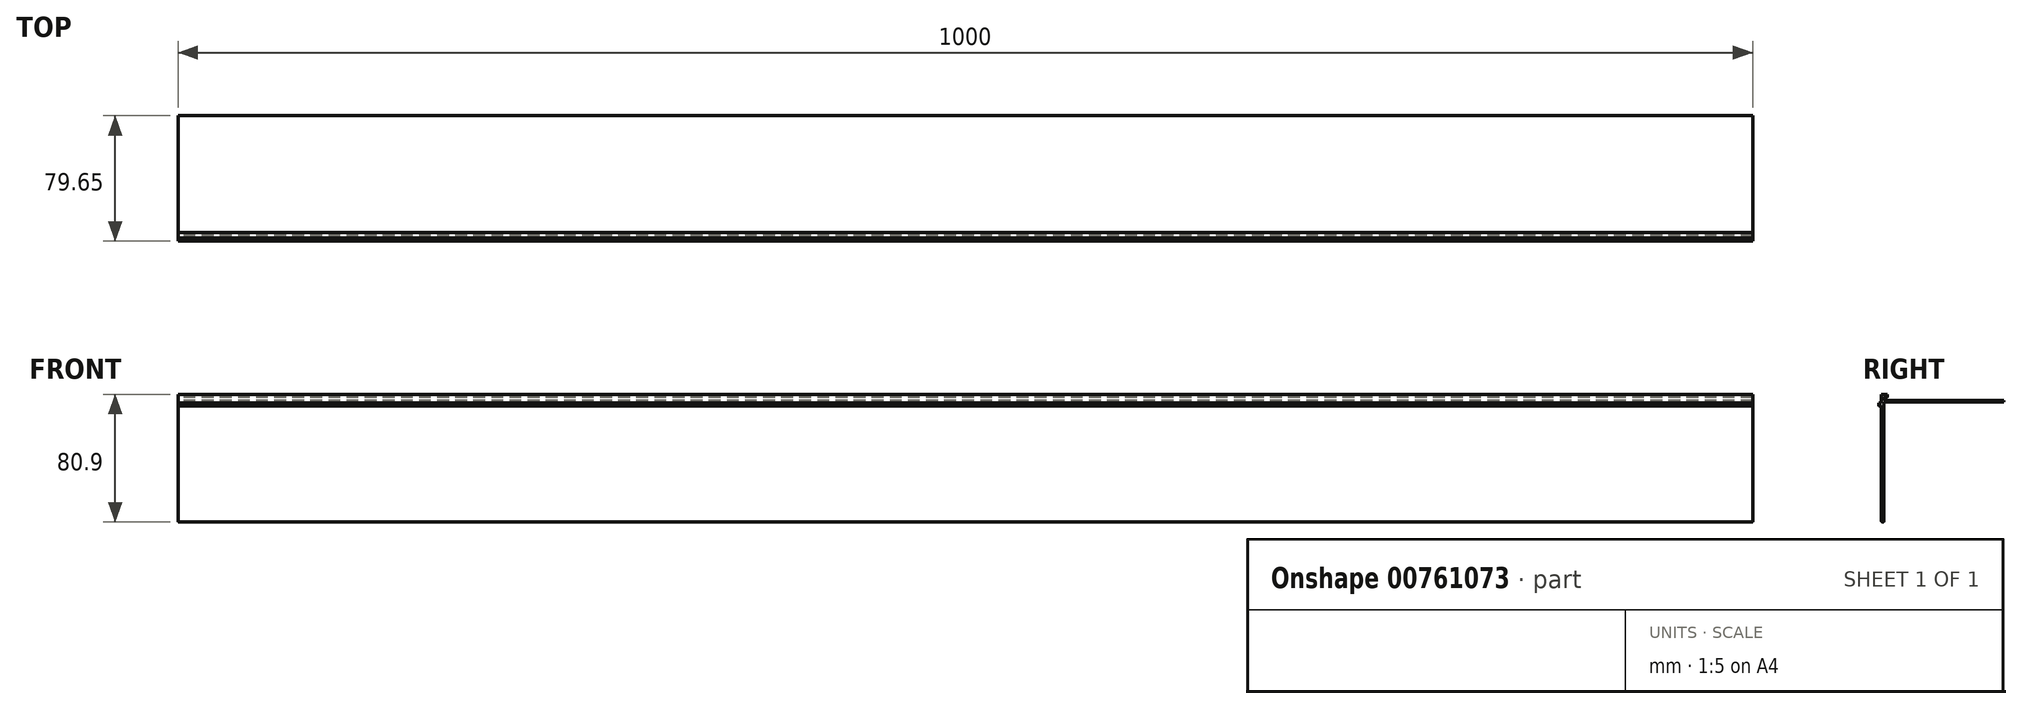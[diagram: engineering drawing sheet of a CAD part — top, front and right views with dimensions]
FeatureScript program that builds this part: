
annotation { "Feature Type Name" : "Feature", "Feature Type Description" : "" }
export const myFeature = defineFeature(function(context is Context, id is Id, definition is map)
    precondition{}
    {
        {
            var Q0;
            Q0=qCreatedBy(makeId("Right.planeOp"),FACE);
            var sketch = newSketch(context, id + "F0", { "sketchPlane" : qUnion([Q0])});
            skLineSegment(sketch, "E0", {"start": v(0, 0.5) * mm, "end": v(0, 73.95) * mm});
            skLineSegment(sketch, "E1", {"start": v(0, 80.9) * mm, "end": v(3.6, 80.9) * mm});
            skLineSegment(sketch, "E2", {"start": v(3.6, 80.9) * mm, "end": v(3.6, 79.3) * mm});
            skPoint(sketch, "E3.endSnap0", {"position": v(-2.18, 15.6) * mm});
            skLineSegment(sketch, "E4", {"start": v(1.6, 79.3) * mm, "end": v(1.6, 77.2) * mm});
            skLineSegment(sketch, "E5", {"start": v(1.6, 77.2) * mm, "end": v(77.8, 77.2) * mm});
            skLineSegment(sketch, "E6", {"start": v(77.8, 77.2) * mm, "end": v(77.8, 76.2) * mm});
            skLineSegment(sketch, "E7", {"start": v(77.8, 76.2) * mm, "end": v(1.6, 76.2) * mm});
            skLineSegment(sketch, "E8", {"start": v(1.6, 76.2) * mm, "end": v(1.6, 0.5) * mm});
            skLineSegment(sketch, "E9", {"start": v(1.1, 0) * mm, "end": v(0.5, 0) * mm});
            skPoint(sketch, "E10.visualSharp", {"position": v(1.6, 0) * mm});
            skArc(sketch, "E10.filletArc", {"start": v(1.1, 0) * mm, "mid": v(1.45, 0.15) * mm, "end": v(1.6, 0.5) * mm});
            skPoint(sketch, "E11.visualSharp", {"position": v(0, 0) * mm});
            skArc(sketch, "E11.filletArc", {"start": v(0, 0.5) * mm, "mid": v(0.15, 0.15) * mm, "end": v(0.5, 0) * mm});
            skLineSegment(sketch, "E12", {"start": v(2.92, 79.05) * mm, "end": v(3.35, 79.05) * mm});
            skLineSegment(sketch, "E13", {"start": v(3.6, 79.3) * mm, "end": v(3.6, 79.3) * mm});
            skPoint(sketch, "E14.visualSharp", {"position": v(2.6, 79.05) * mm});
            skArc(sketch, "E14.filletArc", {"start": v(2.55, 79.3) * mm, "mid": v(2.7, 79.12) * mm, "end": v(2.92, 79.05) * mm});
            skPoint(sketch, "E15.visualSharp", {"position": v(3.6, 79.05) * mm});
            skArc(sketch, "E15.filletArc", {"start": v(3.35, 79.05) * mm, "mid": v(3.52, 79.12) * mm, "end": v(3.6, 79.3) * mm});
            skLineSegment(sketch, "E16", {"start": v(1.6, 79.3) * mm, "end": v(2.55, 79.3) * mm});
            skPoint(sketch, "E17.end.orphan", {"position": v(2.6, 79.3) * mm});
            skLineSegment(sketch, "E18", {"start": v(0, 75.55) * mm, "end": v(-1.85, 75.55) * mm});
            skLineSegment(sketch, "E19", {"start": v(-1.85, 75.55) * mm, "end": v(-1.85, 73.95) * mm});
            skLineSegment(sketch, "E20", {"start": v(-1.6, 73.7) * mm, "end": v(-1.22, 73.7) * mm});
            skLineSegment(sketch, "E21", {"start": v(-0.85, 73.95) * mm, "end": v(0, 73.95) * mm});
            skLineSegment(sketch, "E22.trimOffspring", {"start": v(0, 75.55) * mm, "end": v(0, 80.9) * mm});
            skPoint(sketch, "E23.visualSharp", {"position": v(-0.95, 73.7) * mm});
            skArc(sketch, "E23.filletArc", {"start": v(-1.22, 73.7) * mm, "mid": v(-1, 73.77) * mm, "end": v(-0.85, 73.95) * mm});
            skPoint(sketch, "E24.visualSharp", {"position": v(-1.85, 73.7) * mm});
            skArc(sketch, "E24.filletArc", {"start": v(-1.85, 73.95) * mm, "mid": v(-1.78, 73.77) * mm, "end": v(-1.6, 73.7) * mm});
            skPoint(sketch, "E25.end.orphan", {"position": v(-0.92, 73.95) * mm});
            skSolve(sketch);
        }
        {
            var Q0;
            Q0 = qSketchRegion(id + "F0", true);
            extrude(context, id + "F1", {"entities" : qUnion([Q0]), "depth" : 1000 * mm, "offsetDistance" : 25 * mm});
        }
    });
